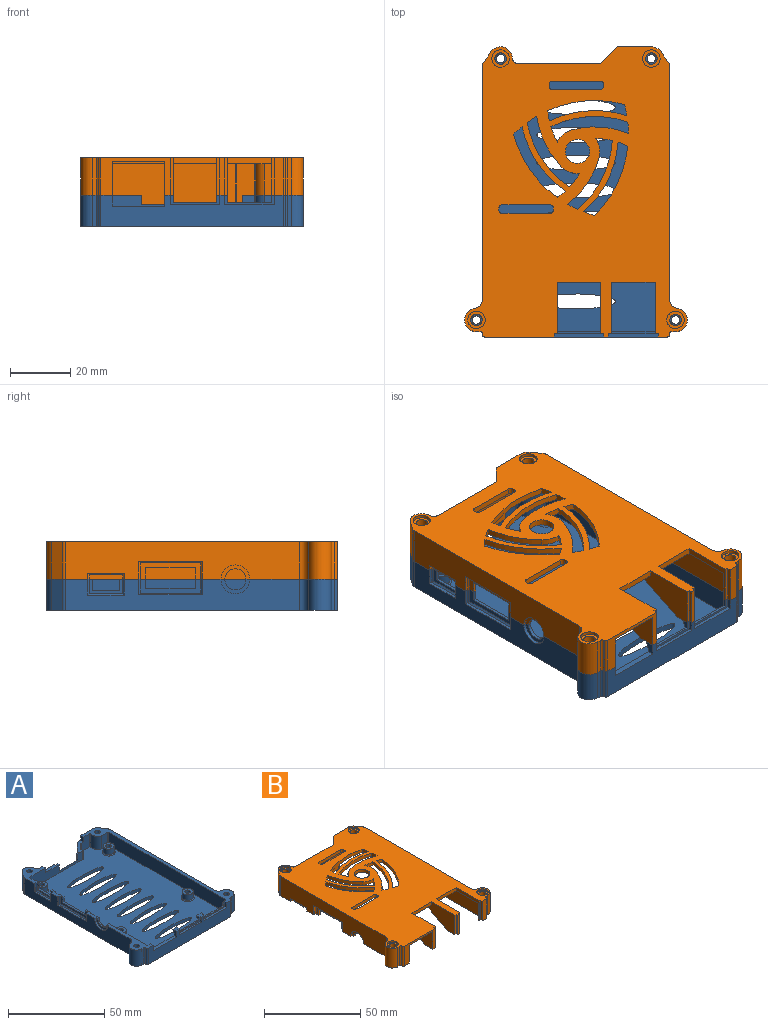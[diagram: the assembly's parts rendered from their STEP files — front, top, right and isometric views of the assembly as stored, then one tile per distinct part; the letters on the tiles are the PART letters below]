
ASSEMBLY  parts=2 mates=1
PART A: 146 faces, bbox 74.1x96.6x10.6 mm
  f0: plane 96.58x74.13mm, normal (0,0,-1), area 5001.7mm2, adj f2,f10,f11,f12,f13,f26,f27,f28
  f1: plane 38.98x8.3mm, normal (0,-1,0), area 190.2mm2, adj f8,f35,f37,f43,f115,f116,f117,f118
  f2: cylinder r=3.9mm len=10.3mm, axis (0,0,-1), area 120.4mm2, adj f0,f5,f107,f114
  f3: plane 3x2.8mm, normal (0,0,1), area 7.2mm2, adj f14,f17,f19,f26,f126,f127
  f4: plane 3.5x3mm, normal (0,0,1), area 8.1mm2, adj f18,f21,f24,f26,f127,f128,f131,f133
  f5: plane 30.25x10.45mm, normal (0,0,1), area 99.5mm2, adj f2,f11,f15,f26,f72,f73,f74,f75
  f6: plane 8.65x2.5mm, normal (0,0,1), area 15.1mm2, adj f73,f77,f79,f80,f81,f82,f84,f85
  f7: plane 9.75x2.5mm, normal (0,0,1), area 16.8mm2, adj f73,f74,f75,f76,f77,f82,f85,f91
  f8: plane 15.1x14.15mm, normal (0,0,1), area 78mm2, adj f1,f10,f33,f73,f77,f81,f83,f84
  f9: plane 96.25x20.25mm, normal (0,0,1), area 280.3mm2, adj f12,f13,f15,f23,f24,f25,f26,f27
  f10: cylinder r=1.4mm len=10.3mm, axis (0,0,-1), area 90.6mm2, adj f0,f8
  f11: cylinder r=1.4mm len=10.3mm, axis (0,0,-1), area 90.6mm2, adj f0,f5
  f12: cylinder r=1.4mm len=10.3mm, axis (0,0,1), area 90.6mm2, adj f0,f9
  f13: cylinder r=1.4mm len=10.3mm, axis (0,0,-1), area 90.6mm2, adj f0,f9
  f14: plane 3.6x3mm, normal (-1,0,0), area 8.7mm2, adj f3,f15,f16,f19,f26,f125
  f15: plane 57x8.3mm, normal (0,1,0), area 322.8mm2, adj f5,f9,f14,f16,f17,f20,f21,f22
  f16: plane 2.8x2mm, normal (0,0.89,-0.45), area 6.3mm2, adj f14,f15,f17,f19
  f17: plane 2.55x1.8mm, normal (1,0,0), area 3.5mm2, adj f3,f15,f16,f19,f127,f132
  f18: plane 3.5x0.55mm, normal (0,1,0), area 1.9mm2, adj f4,f20,f21,f133
  f19: plane 2.8x0.55mm, normal (0,1,0), area 1.5mm2, adj f3,f14,f16,f17
  f20: plane 3.5x2mm, normal (0,0.89,-0.45), area 7.8mm2, adj f15,f18,f21,f133
  f21: plane 2.55x1.8mm, normal (1,0,0), area 3.5mm2, adj f4,f15,f18,f20,f22,f24
  f22: plane 14.5x0.8mm, normal (0,0,1), area 11.6mm2, adj f15,f21,f23,f24
  f23: plane 2.47x0.8mm, normal (-1,0,0), area 2mm2, adj f9,f15,f22,f24
  f24: plane 16.5x3.17mm, normal (0,-1,0), area 16.5mm2, adj f4,f9,f21,f22,f23,f25,f130,f131
  f25: plane 3.17x1.2mm, normal (-1,0,0), area 3.8mm2, adj f9,f24,f26,f130
  f26: plane 60.4x10.3mm, normal (0,-1,0), area 454.9mm2, adj f0,f3,f4,f5,f9,f14,f25,f27
  f27: cylinder r=0.8mm len=10.3mm, axis (0,0,-1), area 12.9mm2, adj f0,f9,f26,f29
  f28: plane 77.46x10.3mm, normal (1,0,0), area 797.8mm2, adj f0,f9,f30,f121
  f29: plane 10.3x0.18mm, normal (1,0,0), area 1.9mm2, adj f0,f9,f27,f123
  f30: cylinder r=2mm len=10.3mm, axis (0,0,1), area 12.6mm2, adj f0,f9,f28,f31
  f31: plane 10.3x3.48mm, normal (0.82,0.58,0), area 43.8mm2, adj f0,f9,f30,f32
  f32: cylinder r=3.9mm len=10.3mm, axis (0,0,-1), area 38.5mm2, adj f0,f9,f31,f135
  f33: plane 27.26x10.3mm, normal (0,1,0), area 101.8mm2, adj f0,f8,f111,f116,f117,f119,f134,f145
  f34: plane 6.3x1mm, normal (-1,0,0), area 5.8mm2, adj f35,f36,f134,f145
  f35: plane 10x7.65mm, normal (0,0,1), area 25.1mm2, adj f1,f34,f36,f37,f39,f134,f135,f136
  f36: plane 16.5x5.3mm, normal (0,1,0), area 22.6mm2, adj f34,f35,f37,f117,f118,f119,f144,f145
  f37: plane 4.8x1mm, normal (-1,0,0), area 4.3mm2, adj f1,f35,f36,f144
  f38: plane 8.3x4.57mm, normal (0,-1,0), area 37.9mm2, adj f9,f40,f43,f139
  f39: plane 3x2mm, normal (-1,0,0), area 6mm2, adj f9,f35,f135,f138
  f40: cylinder r=0.5mm len=8.3mm, axis (0,0,1), area 6.5mm2, adj f9,f38,f41,f43
  f41: plane 85.6x8.3mm, normal (-1,0,0), area 710.5mm2, adj f9,f40,f42,f43
  f42: cylinder r=0.5mm len=8.3mm, axis (0,0,1), area 6.5mm2, adj f9,f15,f41,f43
  f43: plane 92.58x58.33mm, normal (0,0,1), area 4114.6mm2, adj f1,f15,f38,f40,f41,f42,f44,f45
  f44: extruded ~26x5mm, area 109.1mm2, adj f0,f43
  f45: extruded ~26x5mm, area 109.1mm2, adj f0,f43
  f46: extruded ~26x5mm, area 109.1mm2, adj f0,f43
  f47: extruded ~26x5mm, area 109.1mm2, adj f0,f43
  f48: extruded ~26x5mm, area 109.1mm2, adj f0,f43
  f49: extruded ~26x5mm, area 109.1mm2, adj f0,f43
  f50: extruded ~26x5mm, area 109.1mm2, adj f0,f43
  f51: extruded ~26x5mm, area 109.1mm2, adj f0,f43
  f52: cone r=3.15mm half-angle=45deg, axis (0,0,-1), area 14mm2, adj f43,f53
  f53: cylinder r=2.9mm len=5.8mm, axis (0,0,1), area 63.8mm2, adj f52,f55
  f54: plane 5.8x5.8mm, normal (0,0,1), area 20.3mm2, adj f58,f60
  f55: plane 5.8x5.8mm, normal (0,0,1), area 20.3mm2, adj f53,f65
  f56: plane 5.8x5.8mm, normal (0,0,1), area 20.3mm2, adj f67,f68
  f57: plane 5.8x5.8mm, normal (0,0,1), area 20.3mm2, adj f66,f70
  f58: cylinder r=2.9mm len=5.8mm, axis (0,0,1), area 63.8mm2, adj f54,f59
  f59: cone r=3.15mm half-angle=45deg, axis (0,0,-1), area 14mm2, adj f43,f58
  f60: cylinder r=1.4mm len=5mm, axis (0,0,1), area 44mm2, adj f54,f63
  f61: plane 2.8x2.8mm, normal (0,0,1), area 6.2mm2, adj f65
  f62: plane 2.8x2.8mm, normal (0,0,1), area 6.2mm2, adj f66
  f63: plane 2.8x2.8mm, normal (0,0,1), area 6.2mm2, adj f60
  f64: plane 2.8x2.8mm, normal (0,0,1), area 6.2mm2, adj f67
  f65: cylinder r=1.4mm len=5mm, axis (0,0,1), area 44mm2, adj f55,f61
  f66: cylinder r=1.4mm len=5mm, axis (0,0,1), area 44mm2, adj f57,f62
  f67: cylinder r=1.4mm len=5mm, axis (0,0,1), area 44mm2, adj f56,f64
  f68: cylinder r=2.9mm len=5.8mm, axis (0,0,1), area 63.8mm2, adj f56,f69
  f69: cone r=3.15mm half-angle=45deg, axis (0,0,-1), area 14mm2, adj f43,f68
  f70: cylinder r=2.9mm len=5.8mm, axis (0,0,1), area 63.8mm2, adj f57,f71
  f71: cone r=3.15mm half-angle=45deg, axis (0,0,-1), area 14mm2, adj f43,f70
  f72: cylinder r=0.5mm len=8.3mm, axis (0,0,-1), area 6.5mm2, adj f5,f15,f43,f73
  f73: plane 85.6x8.3mm, normal (1,0,0), area 494.1mm2, adj f5,f6,f7,f8,f43,f72,f74,f86
  f74: cylinder r=3.5mm len=7mm, axis (-1,0,0), area 11mm2, adj f5,f7,f73,f75
  f75: plane 9.5x4.75mm, normal (-1,0,0), area 16.2mm2, adj f5,f7,f74,f76
  f76: cylinder r=4.75mm len=9.5mm, axis (-1,0,0), area 14.9mm2, adj f5,f7,f75,f77
  f77: plane 77.46x10.3mm, normal (-1,0,0), area 591.9mm2, adj f0,f5,f6,f7,f8,f76,f79,f98
  f78: plane 10.3x0.18mm, normal (-1,0,0), area 1.9mm2, adj f0,f5,f112,f113
  f79: plane 5.12x1mm, normal (0,-1,0), area 5.1mm2, adj f6,f77,f80,f105
  f80: plane 5.12x0.5mm, normal (-0.71,-0.71,0), area 3.4mm2, adj f6,f79,f82,f106
  f81: plane 11x4.75mm, normal (-1,0,0), area 18.5mm2, adj f6,f8,f83,f89,f90,f97,f100,f101
  f82: plane 20x4.62mm, normal (-1,0,0), area 40.9mm2, adj f6,f7,f80,f91,f92,f93,f103,f106
  f83: plane 3.75x1mm, normal (0,-1,0), area 3.8mm2, adj f8,f81,f84,f90
  f84: plane 14x5.25mm, normal (1,0,0), area 39.8mm2, adj f6,f8,f83,f86,f87,f88,f89,f90
  f85: plane 23x3.62mm, normal (1,0,0), area 31.8mm2, adj f6,f7,f91,f92,f93,f94,f95,f96
  f86: plane 5.75x0.5mm, normal (0.71,0.71,0), area 3.9mm2, adj f8,f73,f84,f87
  f87: plane 15x0.5mm, normal (0.71,0,-0.71), area 10.3mm2, adj f73,f84,f86,f88
  f88: plane 5.75x0.5mm, normal (0.71,-0.71,0), area 3.9mm2, adj f6,f73,f84,f87
  f89: plane 3.75x1mm, normal (0,1,0), area 3.8mm2, adj f6,f81,f84,f90
  f90: plane 9x1mm, normal (0,0,1), area 9mm2, adj f81,f83,f84,f89
  f91: plane 3.12x1mm, normal (0,1,0), area 3.1mm2, adj f7,f82,f85,f92
  f92: plane 16.5x1mm, normal (0,0,1), area 16.5mm2, adj f82,f85,f91,f93
  f93: plane 3.12x1mm, normal (0,-1,0), area 3.1mm2, adj f6,f82,f85,f92
  f94: plane 4.62x0.5mm, normal (0.71,0.71,0), area 2.9mm2, adj f6,f73,f85,f95
  f95: plane 24x1mm, normal (0.89,0,-0.45), area 26.3mm2, adj f73,f85,f94,f96
  f96: plane 4.62x0.5mm, normal (0.71,-0.71,0), area 2.9mm2, adj f7,f73,f85,f95
  f97: plane 5.25x0.5mm, normal (-0.71,0.71,0), area 3.5mm2, adj f6,f81,f98,f100
  f98: plane 5.25x1mm, normal (0,1,0), area 5.2mm2, adj f6,f77,f97,f99
  f99: plane 12x1mm, normal (0,0,1), area 12mm2, adj f77,f98,f100,f102
  f100: plane 12x0.5mm, normal (-0.71,0,0.71), area 8.1mm2, adj f81,f97,f99,f101
  f101: plane 5.25x0.5mm, normal (-0.71,-0.71,0), area 3.5mm2, adj f8,f81,f100,f102
  f102: plane 5.25x1mm, normal (0,-1,0), area 5.2mm2, adj f8,f77,f99,f101
  f103: plane 5.12x0.5mm, normal (-0.71,0.71,0), area 3.4mm2, adj f7,f82,f104,f106
  f104: plane 5.12x1mm, normal (0,1,0), area 5.1mm2, adj f7,f77,f103,f105
  f105: plane 21x1mm, normal (0,0,1), area 21mm2, adj f77,f79,f104,f106
  f106: plane 21x0.5mm, normal (-0.71,0,0.71), area 14.5mm2, adj f80,f82,f103,f105
  f107: cylinder r=3mm len=10.3mm, axis (0,0,-1), area 44mm2, adj f0,f2,f5,f77
  f108: cylinder r=2mm len=10.3mm, axis (0,0,-1), area 12.6mm2, adj f0,f8,f77,f109
  f109: plane 10.3x3.48mm, normal (-0.82,0.58,0), area 43.8mm2, adj f0,f8,f108,f110
  f110: cylinder r=3.9mm len=10.3mm, axis (0,0,-1), area 99.9mm2, adj f0,f8,f109,f111
  f111: cylinder r=2mm len=10.3mm, axis (0,0,-1), area 31.5mm2, adj f0,f8,f33,f110
  f112: cylinder r=0.8mm len=10.3mm, axis (0,0,1), area 12.9mm2, adj f0,f5,f26,f78
  f113: cylinder r=0.8mm len=10.3mm, axis (0,0,1), area 12.9mm2, adj f0,f5,f78,f114
  f114: plane 10.3x1.2mm, normal (0,-1,0), area 12.4mm2, adj f0,f2,f5,f113
  f115: cylinder r=0.5mm len=8.3mm, axis (0,0,1), area 6.5mm2, adj f1,f8,f43,f73
  f116: plane 3x2mm, normal (1,0,0), area 6mm2, adj f1,f8,f33,f117
  f117: plane 10x2mm, normal (0,0,1), area 18.5mm2, adj f1,f33,f36,f116,f118,f119
  f118: plane 4.8x1mm, normal (1,0,0), area 4.3mm2, adj f1,f36,f117,f144
  f119: plane 6.3x1mm, normal (1,0,0), area 5.8mm2, adj f33,f36,f117,f145
  f120: cylinder r=3.9mm len=10.3mm, axis (0,0,1), area 120.4mm2, adj f0,f9,f121,f122
  f121: cylinder r=3mm len=10.3mm, axis (0,0,1), area 44mm2, adj f0,f9,f28,f120
  f122: plane 10.3x1.2mm, normal (0,-1,0), area 12.4mm2, adj f0,f9,f120,f123
  f123: cylinder r=0.8mm len=10.3mm, axis (0,0,-1), area 12.9mm2, adj f0,f9,f29,f122
  f124: plane 3.6x2mm, normal (1,0,0), area 7.2mm2, adj f5,f15,f26,f125
  f125: plane 17.4x2mm, normal (0,0,1), area 34.8mm2, adj f14,f15,f26,f124
  f126: plane 3.17x1.2mm, normal (1,0,0), area 3.8mm2, adj f3,f26,f127,f129
  f127: plane 16.5x3.17mm, normal (0,-1,0), area 16.5mm2, adj f3,f4,f17,f126,f128,f129,f132,f133
  f128: plane 3.17x1.2mm, normal (-1,0,0), area 3.8mm2, adj f4,f26,f127,f129
  f129: plane 16.5x1.2mm, normal (0,0,1), area 19.8mm2, adj f26,f126,f127,f128
  f130: plane 16.5x1.2mm, normal (0,0,1), area 19.8mm2, adj f24,f25,f26,f131
  f131: plane 3.17x1.2mm, normal (1,0,0), area 3.8mm2, adj f4,f24,f26,f130
  f132: plane 14.5x0.8mm, normal (0,0,1), area 11.6mm2, adj f15,f17,f127,f133
  f133: plane 2.55x1.8mm, normal (-1,0,0), area 3.5mm2, adj f4,f15,f18,f20,f127,f132
  f134: plane 7.3x5.65mm, normal (-0.71,0.71,0), area 58.3mm2, adj f0,f33,f34,f35,f135
  f135: plane 11.2x10.3mm, normal (0,1,0), area 106.8mm2, adj f0,f9,f32,f35,f39,f134
  f136: plane 5.3x3.36mm, normal (0.71,-0.71,0), area 25.2mm2, adj f35,f43,f141,f143
  f137: plane 5.3x1.29mm, normal (1,0,0), area 6.9mm2, adj f35,f43,f142,f143
  f138: plane 8.3x5.99mm, normal (0,-1,0), area 44.3mm2, adj f9,f35,f39,f43,f140,f141
  f139: cylinder r=3.9mm len=8.3mm, axis (0,0,1), area 52.3mm2, adj f9,f38,f43,f140
  f140: cylinder r=0.5mm len=8.3mm, axis (0,0,1), area 7.9mm2, adj f9,f43,f138,f139
  f141: cylinder r=0.5mm len=5.3mm, axis (0,0,1), area 2.1mm2, adj f35,f43,f136,f138
  f142: cylinder r=0.5mm len=5.3mm, axis (0,0,-1), area 4.2mm2, adj f1,f35,f43,f137
  f143: cylinder r=0.5mm len=5.3mm, axis (0,0,1), area 2.1mm2, adj f35,f43,f136,f137
  f144: plane 13.5x1mm, normal (0,0.71,0.71), area 19.1mm2, adj f1,f36,f37,f118
  f145: plane 16.5x1mm, normal (0,0.71,0.71), area 23.3mm2, adj f33,f34,f36,f119
PART B: 166 faces, bbox 73.8x96.3x15.5 mm
  f0: plane 8.45x2mm, normal (0,0,-1), area 16.9mm2, adj f4,f62,f67,f70
  f1: plane 96.25x20.3mm, normal (0,0,-1), area 270.4mm2, adj f2,f5,f54,f63,f64,f65,f66,f71
  f2: plane 10.5x4.07mm, normal (0,-1,0), area 42.7mm2, adj f1,f13,f63,f156
  f3: plane 8.45x7.65mm, normal (0,0,-1), area 23.5mm2, adj f62,f66,f69,f154,f155,f157,f158,f159
  f4: plane 27.26x15.5mm, normal (0,1,0), area 374.3mm2, adj f0,f6,f57,f67,f70,f137,f155,f164
  f5: cylinder r=3.9mm len=12.5mm, axis (0,0,1), area 46.7mm2, adj f1,f6,f71,f154
  f6: plane 96.25x73.8mm, normal (0,0,1), area 4510.7mm2, adj f4,f5,f7,f8,f9,f10,f11,f12
  f7: cylinder r=38.11mm len=2.81mm, axis (0,0,1), area 7.6mm2, adj f6,f9,f12,f13
  f8: cylinder r=38.11mm len=3.17mm, axis (0,0,1), area 7.6mm2, adj f6,f13,f33,f34
  f9: cylinder r=34.77mm len=21.39mm, axis (0,0,-1), area 52.8mm2, adj f6,f7,f10,f13
  f10: cylinder r=25.5mm len=2.73mm, axis (0,0,1), area 7mm2, adj f6,f9,f12,f13
  f11: cylinder r=25.5mm len=4.42mm, axis (0,0,1), area 11.1mm2, adj f6,f13,f33,f35
  f12: cylinder r=38.11mm len=21mm, axis (0,0,1), area 52mm2, adj f6,f7,f10,f13
  f13: plane 92.25x58mm, normal (0,0,-1), area 3394.4mm2, adj f2,f7,f8,f9,f10,f11,f12,f14
  f14: cylinder r=38.11mm len=3.71mm, axis (0,0,1), area 7.6mm2, adj f6,f13,f16,f19
  f15: cylinder r=38.11mm len=3.78mm, axis (0,0,1), area 7.6mm2, adj f6,f13,f20,f22
  f16: cylinder r=34.77mm len=25.71mm, axis (0,0,-1), area 52.8mm2, adj f6,f13,f14,f17
  f17: cylinder r=25.5mm len=3.44mm, axis (0,0,1), area 7mm2, adj f6,f13,f16,f19
  f18: cylinder r=25.5mm len=5.08mm, axis (0,0,1), area 11.1mm2, adj f6,f13,f20,f21
  f19: cylinder r=38.11mm len=25.42mm, axis (0,0,1), area 52mm2, adj f6,f13,f14,f17
  f20: cylinder r=32.83mm len=25.5mm, axis (0,0,-1), area 52.5mm2, adj f6,f13,f15,f18
  f21: cylinder r=7.38mm len=4.78mm, axis (0,0,1), area 12.9mm2, adj f6,f13,f18,f22
  f22: cylinder r=29.38mm len=18.77mm, axis (0,0,1), area 38.3mm2, adj f6,f13,f15,f21
  f23: cylinder r=38.11mm len=3.62mm, axis (0,0,1), area 7.6mm2, adj f6,f13,f25,f28
  f24: cylinder r=38.11mm len=3.38mm, axis (0,0,1), area 7.6mm2, adj f6,f13,f29,f31
  f25: cylinder r=34.77mm len=23.14mm, axis (0,0,-1), area 52.8mm2, adj f6,f13,f23,f26
  f26: cylinder r=25.5mm len=3.24mm, axis (0,0,1), area 7mm2, adj f6,f13,f25,f28
  f27: cylinder r=25.5mm len=5.48mm, axis (0,0,1), area 11.1mm2, adj f6,f13,f29,f30
  f28: cylinder r=38.11mm len=23.03mm, axis (0,0,1), area 52mm2, adj f6,f13,f23,f26
  f29: cylinder r=32.83mm len=22.84mm, axis (0,0,-1), area 52.5mm2, adj f6,f13,f24,f27
  f30: cylinder r=7.38mm len=6.15mm, axis (0,0,1), area 12.9mm2, adj f6,f13,f27,f31
  f31: cylinder r=29.38mm len=15.65mm, axis (0,0,1), area 38.3mm2, adj f6,f13,f24,f30
  f32: cylinder r=4mm len=8mm, axis (0,0,1), area 50.3mm2, adj f6,f13
  f33: cylinder r=32.83mm len=21.32mm, axis (0,0,-1), area 52.5mm2, adj f6,f8,f11,f13
  f34: cylinder r=29.38mm len=16.85mm, axis (0,0,1), area 38.3mm2, adj f6,f8,f13,f35
  f35: cylinder r=7.38mm len=5.88mm, axis (0,0,1), area 12.9mm2, adj f6,f11,f13,f34
  f36: plane 16x2mm, normal (0,-1,0), area 32mm2, adj f6,f13,f37,f43
  f37: cylinder r=1mm len=2mm, axis (0,0,-1), area 3.1mm2, adj f6,f13,f36,f38
  f38: plane 2x0.8mm, normal (-1,0,0), area 1.6mm2, adj f6,f13,f37,f39
  f39: cylinder r=1mm len=2mm, axis (0,0,-1), area 3.1mm2, adj f6,f13,f38,f40
  f40: plane 16x2mm, normal (0,1,0), area 32mm2, adj f6,f13,f39,f41
  f41: cylinder r=1mm len=2mm, axis (0,0,-1), area 3.1mm2, adj f6,f13,f40,f42
  f42: plane 2x0.8mm, normal (1,0,0), area 1.6mm2, adj f6,f13,f41,f43
  f43: cylinder r=1mm len=2mm, axis (0,0,-1), area 3.1mm2, adj f6,f13,f36,f42
  f44: plane 2x0.8mm, normal (-1,0,0), area 1.6mm2, adj f6,f13,f45,f51
  f45: cylinder r=1mm len=2mm, axis (0,0,-1), area 3.1mm2, adj f6,f13,f44,f46
  f46: plane 16x2mm, normal (0,1,0), area 32mm2, adj f6,f13,f45,f47
  f47: cylinder r=1mm len=2mm, axis (0,0,-1), area 3.1mm2, adj f6,f13,f46,f48
  f48: plane 2x0.8mm, normal (1,0,0), area 1.6mm2, adj f6,f13,f47,f49
  f49: cylinder r=1mm len=2mm, axis (0,0,-1), area 3.1mm2, adj f6,f13,f48,f50
  f50: plane 16x2mm, normal (0,-1,0), area 32mm2, adj f6,f13,f49,f51
  f51: cylinder r=1mm len=2mm, axis (0,0,-1), area 3.1mm2, adj f6,f13,f44,f50
  f52: cylinder r=1mm len=10.5mm, axis (0,0,-1), area 16.5mm2, adj f13,f53,f56,f60
  f53: plane 10.5x1.55mm, normal (0,1,0), area 16.3mm2, adj f13,f52,f56,f90
  f54: plane 10.5x1.75mm, normal (0,1,0), area 18.4mm2, adj f1,f13,f65,f100
  f55: plane 9.75x2.5mm, normal (0,0,-1), area 16.8mm2, adj f60,f104,f110,f111,f112,f113,f114,f115
  f56: plane 30.25x10.45mm, normal (0,0,-1), area 94.5mm2, adj f52,f53,f60,f82,f90,f103,f104,f105
  f57: plane 32.75x14.2mm, normal (0,0,-1), area 96.1mm2, adj f4,f60,f61,f62,f70,f104,f115,f116
  f58: plane 6x3.5mm, normal (0,0,-1), area 18.6mm2, adj f80,f83,f85,f93,f94,f95,f96,f98
  f59: plane 6x2.8mm, normal (0,0,-1), area 15.6mm2, adj f82,f84,f86,f87,f88,f102
  f60: plane 84.6x10.5mm, normal (1,0,0), area 682.2mm2, adj f13,f52,f55,f56,f57,f61,f112,f122
  f61: cylinder r=1mm len=10.5mm, axis (0,0,1), area 16.5mm2, adj f13,f57,f60,f62
  f62: plane 38.48x13.5mm, normal (0,-1,0), area 485.9mm2, adj f0,f3,f13,f57,f61,f70,f163,f165
  f63: cylinder r=1mm len=10.5mm, axis (0,0,1), area 16.5mm2, adj f1,f2,f13,f64
  f64: plane 84.6x10.5mm, normal (-1,0,0), area 888.3mm2, adj f1,f13,f63,f65
  f65: cylinder r=1mm len=10.5mm, axis (0,0,1), area 16.5mm2, adj f1,f13,f54,f64
  f66: plane 3x2mm, normal (1,0,0), area 6mm2, adj f1,f3,f154,f157
  f67: plane 2.5x2mm, normal (1,0,0), area 2.5mm2, adj f0,f4,f68,f164,f165
  f68: plane 16.5x0.5mm, normal (0,1,0), area 8.3mm2, adj f67,f69,f164,f165
  f69: plane 2.5x2mm, normal (-1,0,0), area 2.5mm2, adj f3,f68,f155,f164,f165
  f70: plane 3x2mm, normal (-1,0,0), area 6mm2, adj f0,f4,f57,f62
  f71: plane 12.5x3.48mm, normal (0.82,0.58,0), area 53.1mm2, adj f1,f5,f6,f72
  f72: cylinder r=2mm len=12.5mm, axis (0,0,1), area 15.3mm2, adj f1,f6,f71,f73
  f73: plane 77.46x12.5mm, normal (1,0,0), area 968.2mm2, adj f1,f6,f72,f75
  f74: plane 12.5x0.18mm, normal (1,0,0), area 2.3mm2, adj f1,f6,f78,f79
  f75: cylinder r=3mm len=12.5mm, axis (0,0,1), area 53.5mm2, adj f1,f6,f73,f76
  f76: cylinder r=3.9mm len=12.5mm, axis (0,0,1), area 146.1mm2, adj f1,f6,f75,f77
  f77: plane 12.5x1.2mm, normal (0,-1,0), area 15mm2, adj f1,f6,f76,f78
  f78: cylinder r=0.8mm len=12.5mm, axis (0,0,-1), area 15.7mm2, adj f1,f6,f74,f77
  f79: cylinder r=0.8mm len=12.5mm, axis (0,0,-1), area 15.7mm2, adj f1,f6,f74,f81
  f80: plane 12.5x1.5mm, normal (0,-1,0), area 18.8mm2, adj f6,f58,f83,f98
  f81: plane 12.5x2.95mm, normal (0,-1,0), area 36.9mm2, adj f1,f6,f79,f99
  f82: plane 22.95x12.5mm, normal (0,-1,0), area 90.3mm2, adj f6,f56,f59,f88,f90,f91,f102,f103
  f83: plane 12.5x1.2mm, normal (-1,0,0), area 15mm2, adj f6,f58,f80,f85
  f84: plane 12.5x1mm, normal (0,-1,0), area 12.5mm2, adj f6,f59,f86,f102
  f85: plane 12.5x1mm, normal (0,-1,0), area 12.5mm2, adj f6,f58,f83,f93
  f86: plane 25.8x12.5mm, normal (1,0,0), area 194.7mm2, adj f6,f13,f59,f84,f87,f92
  f87: plane 21x10.5mm, normal (0,0.45,-0.89), area 65.7mm2, adj f13,f59,f86,f88
  f88: plane 27x11.3mm, normal (-1,0,0), area 191.4mm2, adj f13,f59,f82,f87,f89,f91
  f89: plane 17.4x0.8mm, normal (0,-1,0), area 13.9mm2, adj f13,f88,f90,f91
  f90: plane 22.7x11.3mm, normal (1,0,0), area 39.2mm2, adj f13,f53,f56,f82,f89,f91
  f91: plane 22.7x17.4mm, normal (0,0,-1), area 395mm2, adj f82,f88,f89,f90
  f92: plane 14.5x2mm, normal (0,-1,0), area 29mm2, adj f6,f13,f86,f93
  f93: plane 25.8x12.5mm, normal (-1,0,0), area 194.7mm2, adj f6,f13,f58,f85,f92,f94
  f94: plane 21x10.5mm, normal (0,0.45,-0.89), area 82.2mm2, adj f13,f58,f93,f95
  f95: plane 25.8x12.5mm, normal (1,0,0), area 194.7mm2, adj f6,f13,f58,f94,f96,f101
  f96: plane 12.5x1mm, normal (0,-1,0), area 12.5mm2, adj f6,f58,f95,f98
  f97: plane 12.5x1mm, normal (0,-1,0), area 12.5mm2, adj f1,f6,f99,f100
  f98: plane 12.5x1.2mm, normal (1,0,0), area 15mm2, adj f6,f58,f80,f96
  f99: plane 12.5x1.2mm, normal (-1,0,0), area 15mm2, adj f1,f6,f81,f97
  f100: plane 17.05x12.5mm, normal (-1,0,0), area 42.5mm2, adj f1,f6,f13,f54,f97,f101
  f101: plane 14.5x2mm, normal (0,-1,0), area 29mm2, adj f6,f13,f95,f100
  f102: plane 12.5x1.2mm, normal (1,0,0), area 15mm2, adj f6,f59,f82,f84
  f103: cylinder r=0.8mm len=12.5mm, axis (0,0,1), area 15.7mm2, adj f6,f56,f82,f105
  f104: plane 77.46x12.5mm, normal (-1,0,0), area 784.3mm2, adj f6,f55,f56,f57,f106,f110,f113,f117
  f105: plane 12.5x0.18mm, normal (-1,0,0), area 2.2mm2, adj f6,f56,f103,f109
  f106: cylinder r=3mm len=12.5mm, axis (0,0,-1), area 53.5mm2, adj f6,f56,f104,f107
  f107: cylinder r=3.9mm len=12.5mm, axis (0,0,1), area 146.1mm2, adj f6,f56,f106,f108
  f108: plane 12.5x1.2mm, normal (0,-1,0), area 15mm2, adj f6,f56,f107,f109
  f109: cylinder r=0.8mm len=12.5mm, axis (0,0,1), area 15.7mm2, adj f6,f56,f105,f108
  f110: cylinder r=4.75mm len=9.5mm, axis (-1,0,0), area 14.9mm2, adj f55,f56,f104,f111
  f111: plane 9.5x4.75mm, normal (-1,0,0), area 16.2mm2, adj f55,f56,f110,f112
  f112: cylinder r=3.5mm len=7mm, axis (-1,0,0), area 11mm2, adj f55,f56,f60,f111
  f113: plane 5.93x1mm, normal (0,1,0), area 5.9mm2, adj f55,f104,f114,f118
  f114: plane 5.93x0.5mm, normal (-0.71,0.71,0), area 4mm2, adj f55,f113,f115,f119
  f115: plane 20x5.43mm, normal (-1,0,0), area 43.8mm2, adj f55,f57,f114,f116,f119,f120,f125,f126
  f116: plane 5.93x0.5mm, normal (-0.71,-0.71,0), area 4mm2, adj f57,f115,f117,f119
  f117: plane 5.93x1mm, normal (0,-1,0), area 5.9mm2, adj f57,f104,f116,f118
  f118: plane 21x1mm, normal (0,0,-1), area 21mm2, adj f104,f113,f117,f119
  f119: plane 21x0.5mm, normal (-0.71,0,-0.71), area 14.5mm2, adj f114,f115,f116,f118
  f120: plane 3.93x1mm, normal (0,1,0), area 3.9mm2, adj f55,f115,f121,f126
  f121: plane 23x5.93mm, normal (1,0,0), area 71.5mm2, adj f55,f57,f120,f122,f123,f124,f125,f126
  f122: plane 6.43x0.5mm, normal (0.71,-0.71,0), area 4.4mm2, adj f55,f60,f121,f123
  f123: plane 24x0.5mm, normal (0.71,0,0.71), area 16.6mm2, adj f60,f121,f122,f124
  f124: plane 6.43x0.5mm, normal (0.71,0.71,0), area 4.4mm2, adj f57,f60,f121,f123
  f125: plane 3.93x1mm, normal (0,-1,0), area 3.9mm2, adj f57,f115,f121,f126
  f126: plane 16.5x1mm, normal (0,0,-1), area 16.5mm2, adj f115,f120,f121,f125
  f127: plane 2x1mm, normal (0,1,0), area 2mm2, adj f57,f104,f128,f132
  f128: plane 2x0.5mm, normal (-0.71,0.71,0), area 1.2mm2, adj f57,f127,f129,f133
  f129: plane 11x1.5mm, normal (-1,0,0), area 16.5mm2, adj f57,f128,f130,f133
  f130: plane 2x0.5mm, normal (-0.71,-0.71,0), area 1.2mm2, adj f57,f129,f131,f133
  f131: plane 2x1mm, normal (0,-1,0), area 2mm2, adj f57,f104,f130,f132
  f132: plane 12x1mm, normal (0,0,-1), area 12mm2, adj f104,f127,f131,f133
  f133: plane 12x0.5mm, normal (-0.71,0,-0.71), area 8.1mm2, adj f128,f129,f130,f132
  f134: cylinder r=2mm len=12.5mm, axis (0,0,-1), area 15.3mm2, adj f6,f57,f104,f135
  f135: plane 12.5x3.48mm, normal (-0.82,0.58,0), area 53.1mm2, adj f6,f57,f134,f136
  f136: cylinder r=3.9mm len=12.5mm, axis (0,0,1), area 121.2mm2, adj f6,f57,f135,f137
  f137: cylinder r=2mm len=12.5mm, axis (0,0,-1), area 38.2mm2, adj f4,f6,f57,f136
  f138: plane 2.5x0.5mm, normal (0.71,0.71,0), area 1.6mm2, adj f57,f60,f139,f141
  f139: plane 12x2mm, normal (1,0,0), area 24mm2, adj f57,f138,f140,f141
  f140: plane 2.5x0.5mm, normal (0.71,-0.71,0), area 1.6mm2, adj f57,f60,f139,f141
  f141: plane 13x0.5mm, normal (0.71,0,0.71), area 8.8mm2, adj f60,f138,f139,f140
  f142: cylinder r=1.9mm len=11.5mm, axis (0,0,1), area 137.3mm2, adj f1,f145
  f143: plane 5.8x5.8mm, normal (0,0,1), area 15.1mm2, adj f147,f153
  f144: plane 5.8x5.8mm, normal (0,0,1), area 15.1mm2, adj f148,f152
  f145: plane 5.8x5.8mm, normal (0,0,1), area 15.1mm2, adj f142,f149
  f146: plane 5.8x5.8mm, normal (0,0,1), area 15.1mm2, adj f150,f151
  f147: cylinder r=2.9mm len=5.8mm, axis (0,0,1), area 18.2mm2, adj f6,f143
  f148: cylinder r=2.9mm len=5.8mm, axis (0,0,1), area 18.2mm2, adj f6,f144
  f149: cylinder r=2.9mm len=5.8mm, axis (0,0,1), area 18.2mm2, adj f6,f145
  f150: cylinder r=2.9mm len=5.8mm, axis (0,0,1), area 18.2mm2, adj f6,f146
  f151: cylinder r=1.9mm len=11.5mm, axis (0,0,1), area 137.3mm2, adj f56,f146
  f152: cylinder r=1.9mm len=11.5mm, axis (0,0,-1), area 137.3mm2, adj f1,f144
  f153: cylinder r=1.9mm len=11.5mm, axis (0,0,-1), area 137.3mm2, adj f57,f143
  f154: plane 15.5x11.2mm, normal (0,1,0), area 148.4mm2, adj f1,f3,f5,f6,f66,f155
  f155: plane 15.5x5.65mm, normal (-0.71,0.71,0), area 123.8mm2, adj f3,f4,f6,f69,f154
  f156: cylinder r=3.9mm len=10.5mm, axis (0,0,-1), area 66.2mm2, adj f1,f2,f13,f162
  f157: plane 13.5x5.99mm, normal (0,-1,0), area 68.2mm2, adj f1,f3,f13,f66,f161,f162
  f158: plane 13.5x1.29mm, normal (1,0,0), area 17.5mm2, adj f3,f13,f160,f163
  f159: plane 13.5x3.36mm, normal (0.71,-0.71,0), area 64.1mm2, adj f3,f13,f160,f161
  f160: cylinder r=0.5mm len=13.5mm, axis (0,0,-1), area 5.3mm2, adj f3,f13,f158,f159
  f161: cylinder r=0.5mm len=13.5mm, axis (0,0,1), area 5.3mm2, adj f3,f13,f157,f159
  f162: cylinder r=0.5mm len=10.5mm, axis (0,0,-1), area 9.9mm2, adj f1,f13,f156,f157
  f163: cylinder r=0.5mm len=13.5mm, axis (0,0,-1), area 10.6mm2, adj f3,f13,f62,f158
  f164: plane 16.5x1mm, normal (0,0.71,-0.71), area 23.3mm2, adj f4,f67,f68,f69
  f165: plane 16.5x1mm, normal (0,0.71,-0.71), area 23.3mm2, adj f62,f67,f68,f69
PLACE A t=(80.15,-5.97,4.07)mm fixed
PLACE B t=(80.15,-5.97,24.87)mm
MATE slider A.f2 <-> B.f107  axis (0,0,1) through (78.15,4.11,14.37)mm
